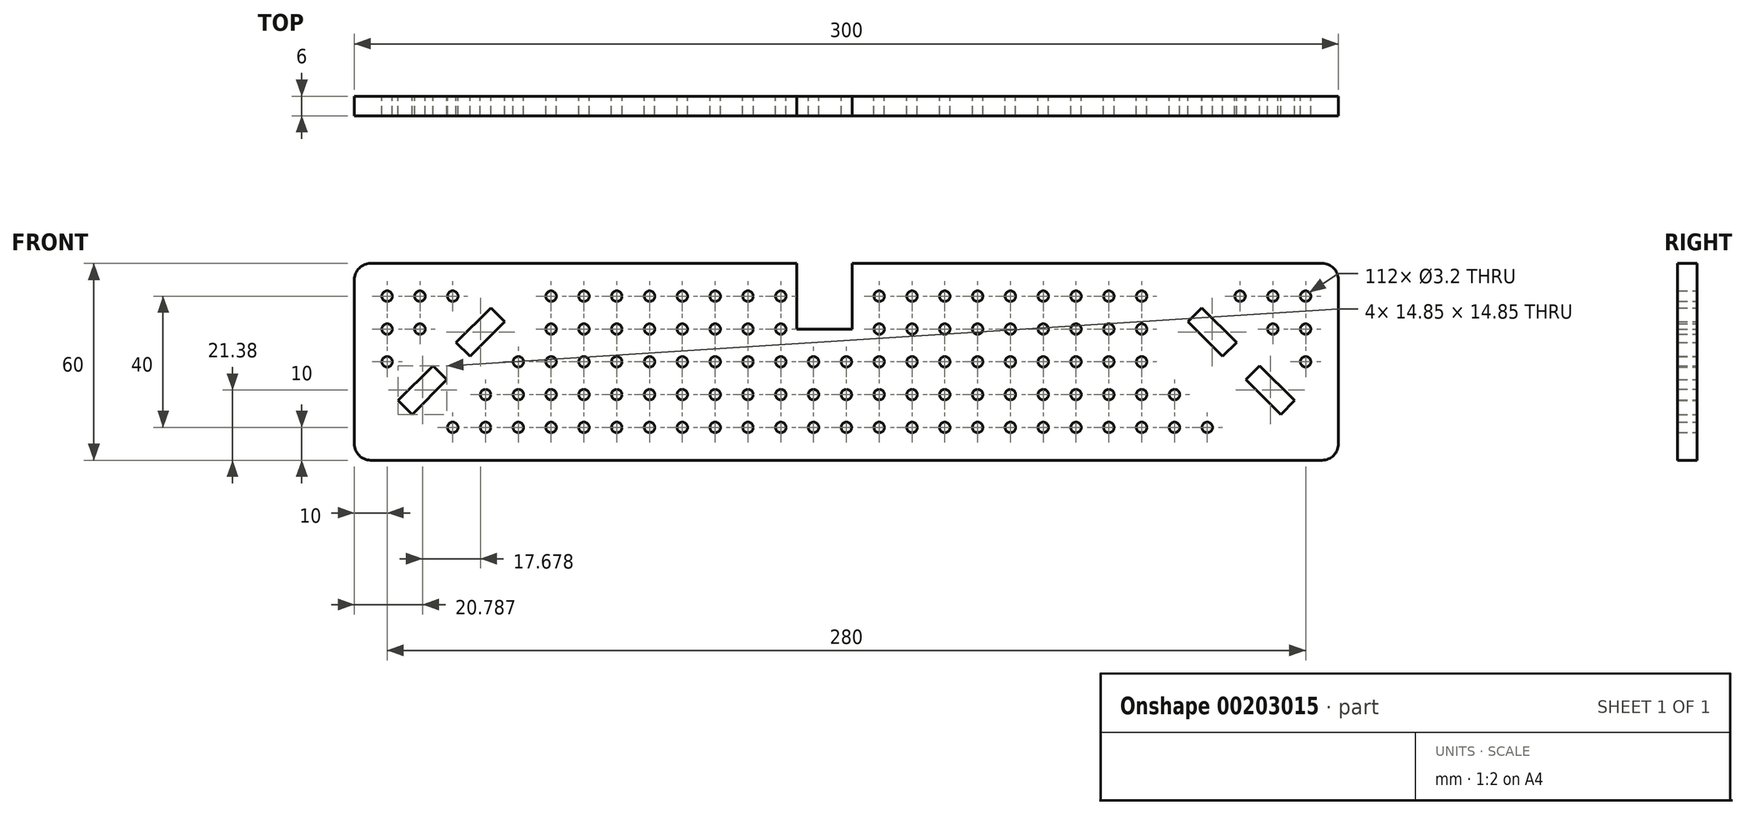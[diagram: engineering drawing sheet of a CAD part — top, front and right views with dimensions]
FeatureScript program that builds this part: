
annotation { "Feature Type Name" : "Feature", "Feature Type Description" : "" }
export const myFeature = defineFeature(function(context is Context, id is Id, definition is map)
    precondition{}
    {
        {
            var Q0;
            Q0=qCreatedBy(makeId("Front.planeOp"),FACE);
            var sketch = newSketch(context, id + "F0", { "sketchPlane" : qUnion([Q0])});
            skLineSegment(sketch, "E0", {"start": v(-150, -25) * mm, "end": v(-150, 25) * mm});
            skArc(sketch, "E1", {"start": v(-150, 25) * mm, "mid": v(-148.54, 28.54) * mm, "end": v(-145, 30) * mm});
            skLineSegment(sketch, "E2", {"start": v(-145, 30) * mm, "end": v(-15.18, 30) * mm});
            skArc(sketch, "E3", {"start": v(145, 30) * mm, "mid": v(148.54, 28.54) * mm, "end": v(150, 25) * mm});
            skLineSegment(sketch, "E4", {"start": v(150, 25) * mm, "end": v(150, -25) * mm});
            skArc(sketch, "E5", {"start": v(150, -25) * mm, "mid": v(148.54, -28.54) * mm, "end": v(145, -30) * mm});
            skLineSegment(sketch, "E6", {"start": v(145, -30) * mm, "end": v(-145, -30) * mm});
            skArc(sketch, "E7", {"start": v(-145, -30) * mm, "mid": v(-148.54, -28.54) * mm, "end": v(-150, -25) * mm});
            skLineSegment(sketch, "E8", {"start": v(-126.03, -1.2) * mm, "end": v(-136.64, -11.8) * mm});
            skLineSegment(sketch, "E9", {"start": v(-136.64, -11.8) * mm, "end": v(-132.4, -16.04) * mm});
            skLineSegment(sketch, "E10", {"start": v(-132.4, -16.04) * mm, "end": v(-121.79, -5.44) * mm});
            skLineSegment(sketch, "E11", {"start": v(-121.79, -5.44) * mm, "end": v(-126.03, -1.2) * mm});
            skLineSegment(sketch, "E12", {"start": v(-108.35, 16.48) * mm, "end": v(-118.96, 5.88) * mm});
            skLineSegment(sketch, "E13", {"start": v(-118.96, 5.88) * mm, "end": v(-114.72, 1.63) * mm});
            skLineSegment(sketch, "E14", {"start": v(-114.72, 1.63) * mm, "end": v(-104.11, 12.24) * mm});
            skLineSegment(sketch, "E15", {"start": v(-104.11, 12.24) * mm, "end": v(-108.35, 16.48) * mm});
            skCircle(sketch, "E16", {"center": v(-120, -20) * mm, "radius": 1.6 * mm});
            skCircle(sketch, "E17", {"center": v(-110, -20) * mm, "radius": 1.6 * mm});
            skCircle(sketch, "E18", {"center": v(-100, -20) * mm, "radius": 1.6 * mm});
            skCircle(sketch, "E19", {"center": v(-90, -20) * mm, "radius": 1.6 * mm});
            skCircle(sketch, "E20", {"center": v(-80, -20) * mm, "radius": 1.6 * mm});
            skCircle(sketch, "E21", {"center": v(-70, -20) * mm, "radius": 1.6 * mm});
            skCircle(sketch, "E22", {"center": v(-60, -20) * mm, "radius": 1.6 * mm});
            skCircle(sketch, "E23", {"center": v(-50, -20) * mm, "radius": 1.6 * mm});
            skCircle(sketch, "E24", {"center": v(-40, -20) * mm, "radius": 1.6 * mm});
            skCircle(sketch, "E25", {"center": v(-30, -20) * mm, "radius": 1.6 * mm});
            skCircle(sketch, "E26", {"center": v(-20, -20) * mm, "radius": 1.6 * mm});
            skCircle(sketch, "E27", {"center": v(-10, -20) * mm, "radius": 1.6 * mm});
            skCircle(sketch, "E28", {"center": v(0, -20) * mm, "radius": 1.6 * mm});
            skCircle(sketch, "E29", {"center": v(10, -20) * mm, "radius": 1.6 * mm});
            skCircle(sketch, "E30", {"center": v(20, -20) * mm, "radius": 1.6 * mm});
            skCircle(sketch, "E31", {"center": v(30, -20) * mm, "radius": 1.6 * mm});
            skCircle(sketch, "E32", {"center": v(40, -20) * mm, "radius": 1.6 * mm});
            skCircle(sketch, "E33", {"center": v(50, -20) * mm, "radius": 1.6 * mm});
            skCircle(sketch, "E34", {"center": v(60, -20) * mm, "radius": 1.6 * mm});
            skCircle(sketch, "E35", {"center": v(70, -20) * mm, "radius": 1.6 * mm});
            skCircle(sketch, "E36", {"center": v(80, -20) * mm, "radius": 1.6 * mm});
            skCircle(sketch, "E37", {"center": v(90, -20) * mm, "radius": 1.6 * mm});
            skCircle(sketch, "E38", {"center": v(100, -20) * mm, "radius": 1.6 * mm});
            skCircle(sketch, "E39", {"center": v(110, -20) * mm, "radius": 1.6 * mm});
            skCircle(sketch, "E40", {"center": v(-110, -10) * mm, "radius": 1.6 * mm});
            skCircle(sketch, "E41", {"center": v(-100, -10) * mm, "radius": 1.6 * mm});
            skCircle(sketch, "E42", {"center": v(-90, -10) * mm, "radius": 1.6 * mm});
            skCircle(sketch, "E43", {"center": v(-80, -10) * mm, "radius": 1.6 * mm});
            skCircle(sketch, "E44", {"center": v(-70, -10) * mm, "radius": 1.6 * mm});
            skCircle(sketch, "E45", {"center": v(-60, -10) * mm, "radius": 1.6 * mm});
            skCircle(sketch, "E46", {"center": v(-50, -10) * mm, "radius": 1.6 * mm});
            skCircle(sketch, "E47", {"center": v(-40, -10) * mm, "radius": 1.6 * mm});
            skCircle(sketch, "E48", {"center": v(-30, -10) * mm, "radius": 1.6 * mm});
            skCircle(sketch, "E49", {"center": v(-20, -10) * mm, "radius": 1.6 * mm});
            skCircle(sketch, "E50", {"center": v(-10, -10) * mm, "radius": 1.6 * mm});
            skCircle(sketch, "E51", {"center": v(0, -10) * mm, "radius": 1.6 * mm});
            skCircle(sketch, "E52", {"center": v(10, -10) * mm, "radius": 1.6 * mm});
            skCircle(sketch, "E53", {"center": v(20, -10) * mm, "radius": 1.6 * mm});
            skCircle(sketch, "E54", {"center": v(30, -10) * mm, "radius": 1.6 * mm});
            skCircle(sketch, "E55", {"center": v(40, -10) * mm, "radius": 1.6 * mm});
            skCircle(sketch, "E56", {"center": v(50, -10) * mm, "radius": 1.6 * mm});
            skCircle(sketch, "E57", {"center": v(60, -10) * mm, "radius": 1.6 * mm});
            skCircle(sketch, "E58", {"center": v(70, -10) * mm, "radius": 1.6 * mm});
            skCircle(sketch, "E59", {"center": v(80, -10) * mm, "radius": 1.6 * mm});
            skCircle(sketch, "E60", {"center": v(90, -10) * mm, "radius": 1.6 * mm});
            skCircle(sketch, "E61", {"center": v(100, -10) * mm, "radius": 1.6 * mm});
            skCircle(sketch, "E62", {"center": v(-140, 0) * mm, "radius": 1.6 * mm});
            skCircle(sketch, "E63", {"center": v(-100, 0) * mm, "radius": 1.6 * mm});
            skCircle(sketch, "E64", {"center": v(-90, 0) * mm, "radius": 1.6 * mm});
            skCircle(sketch, "E65", {"center": v(-80, 0) * mm, "radius": 1.6 * mm});
            skCircle(sketch, "E66", {"center": v(-70, 0) * mm, "radius": 1.6 * mm});
            skCircle(sketch, "E67", {"center": v(-60, 0) * mm, "radius": 1.6 * mm});
            skCircle(sketch, "E68", {"center": v(-50, 0) * mm, "radius": 1.6 * mm});
            skCircle(sketch, "E69", {"center": v(-40, 0) * mm, "radius": 1.6 * mm});
            skCircle(sketch, "E70", {"center": v(-30, 0) * mm, "radius": 1.6 * mm});
            skCircle(sketch, "E71", {"center": v(-20, 0) * mm, "radius": 1.6 * mm});
            skCircle(sketch, "E72", {"center": v(-10, 0) * mm, "radius": 1.6 * mm});
            skCircle(sketch, "E73", {"center": v(0, 0) * mm, "radius": 1.6 * mm});
            skCircle(sketch, "E74", {"center": v(10, 0) * mm, "radius": 1.6 * mm});
            skCircle(sketch, "E75", {"center": v(20, 0) * mm, "radius": 1.6 * mm});
            skCircle(sketch, "E76", {"center": v(30, 0) * mm, "radius": 1.6 * mm});
            skCircle(sketch, "E77", {"center": v(40, 0) * mm, "radius": 1.6 * mm});
            skCircle(sketch, "E78", {"center": v(50, 0) * mm, "radius": 1.6 * mm});
            skCircle(sketch, "E79", {"center": v(60, 0) * mm, "radius": 1.6 * mm});
            skCircle(sketch, "E80", {"center": v(70, 0) * mm, "radius": 1.6 * mm});
            skCircle(sketch, "E81", {"center": v(80, 0) * mm, "radius": 1.6 * mm});
            skCircle(sketch, "E82", {"center": v(90, 0) * mm, "radius": 1.6 * mm});
            skCircle(sketch, "E83", {"center": v(140, 0) * mm, "radius": 1.6 * mm});
            skCircle(sketch, "E84", {"center": v(-140, 10) * mm, "radius": 1.6 * mm});
            skCircle(sketch, "E85", {"center": v(-130, 10) * mm, "radius": 1.6 * mm});
            skCircle(sketch, "E86", {"center": v(-90, 10) * mm, "radius": 1.6 * mm});
            skCircle(sketch, "E87", {"center": v(-80, 10) * mm, "radius": 1.6 * mm});
            skCircle(sketch, "E88", {"center": v(-70, 10) * mm, "radius": 1.6 * mm});
            skCircle(sketch, "E89", {"center": v(-60, 10) * mm, "radius": 1.6 * mm});
            skCircle(sketch, "E90", {"center": v(-50, 10) * mm, "radius": 1.6 * mm});
            skCircle(sketch, "E91", {"center": v(-40, 10) * mm, "radius": 1.6 * mm});
            skCircle(sketch, "E92", {"center": v(-30, 10) * mm, "radius": 1.6 * mm});
            skCircle(sketch, "E93", {"center": v(-20, 10) * mm, "radius": 1.6 * mm});
            skCircle(sketch, "E94", {"center": v(10, 10) * mm, "radius": 1.6 * mm});
            skCircle(sketch, "E95", {"center": v(20, 10) * mm, "radius": 1.6 * mm});
            skCircle(sketch, "E96", {"center": v(30, 10) * mm, "radius": 1.6 * mm});
            skCircle(sketch, "E97", {"center": v(40, 10) * mm, "radius": 1.6 * mm});
            skCircle(sketch, "E98", {"center": v(50, 10) * mm, "radius": 1.6 * mm});
            skCircle(sketch, "E99", {"center": v(60, 10) * mm, "radius": 1.6 * mm});
            skCircle(sketch, "E100", {"center": v(70, 10) * mm, "radius": 1.6 * mm});
            skCircle(sketch, "E101", {"center": v(80, 10) * mm, "radius": 1.6 * mm});
            skCircle(sketch, "E102", {"center": v(90, 10) * mm, "radius": 1.6 * mm});
            skCircle(sketch, "E103", {"center": v(130, 10) * mm, "radius": 1.6 * mm});
            skCircle(sketch, "E104", {"center": v(140, 10) * mm, "radius": 1.6 * mm});
            skCircle(sketch, "E105", {"center": v(-140, 20) * mm, "radius": 1.6 * mm});
            skCircle(sketch, "E106", {"center": v(-130, 20) * mm, "radius": 1.6 * mm});
            skCircle(sketch, "E107", {"center": v(-120, 20) * mm, "radius": 1.6 * mm});
            skCircle(sketch, "E108", {"center": v(-90, 20) * mm, "radius": 1.6 * mm});
            skCircle(sketch, "E109", {"center": v(-80, 20) * mm, "radius": 1.6 * mm});
            skCircle(sketch, "E110", {"center": v(-70, 20) * mm, "radius": 1.6 * mm});
            skCircle(sketch, "E111", {"center": v(-60, 20) * mm, "radius": 1.6 * mm});
            skCircle(sketch, "E112", {"center": v(-50, 20) * mm, "radius": 1.6 * mm});
            skCircle(sketch, "E113", {"center": v(-40, 20) * mm, "radius": 1.6 * mm});
            skCircle(sketch, "E114", {"center": v(-30, 20) * mm, "radius": 1.6 * mm});
            skCircle(sketch, "E115", {"center": v(-20, 20) * mm, "radius": 1.6 * mm});
            skCircle(sketch, "E116", {"center": v(10, 20) * mm, "radius": 1.6 * mm});
            skCircle(sketch, "E117", {"center": v(20, 20) * mm, "radius": 1.6 * mm});
            skCircle(sketch, "E118", {"center": v(30, 20) * mm, "radius": 1.6 * mm});
            skCircle(sketch, "E119", {"center": v(40, 20) * mm, "radius": 1.6 * mm});
            skCircle(sketch, "E120", {"center": v(50, 20) * mm, "radius": 1.6 * mm});
            skCircle(sketch, "E121", {"center": v(60, 20) * mm, "radius": 1.6 * mm});
            skCircle(sketch, "E122", {"center": v(70, 20) * mm, "radius": 1.6 * mm});
            skCircle(sketch, "E123", {"center": v(80, 20) * mm, "radius": 1.6 * mm});
            skCircle(sketch, "E124", {"center": v(90, 20) * mm, "radius": 1.6 * mm});
            skCircle(sketch, "E125", {"center": v(120, 20) * mm, "radius": 1.6 * mm});
            skCircle(sketch, "E126", {"center": v(130, 20) * mm, "radius": 1.6 * mm});
            skCircle(sketch, "E127", {"center": v(140, 20) * mm, "radius": 1.6 * mm});
            skLineSegment(sketch, "E128", {"start": v(126.03, -1.2) * mm, "end": v(136.64, -11.8) * mm});
            skLineSegment(sketch, "E129", {"start": v(136.64, -11.8) * mm, "end": v(132.4, -16.04) * mm});
            skLineSegment(sketch, "E130", {"start": v(132.4, -16.04) * mm, "end": v(121.79, -5.44) * mm});
            skLineSegment(sketch, "E131", {"start": v(121.79, -5.44) * mm, "end": v(126.03, -1.2) * mm});
            skLineSegment(sketch, "E132", {"start": v(108.35, 16.48) * mm, "end": v(118.96, 5.88) * mm});
            skLineSegment(sketch, "E133", {"start": v(118.96, 5.88) * mm, "end": v(114.72, 1.63) * mm});
            skLineSegment(sketch, "E134", {"start": v(114.72, 1.63) * mm, "end": v(104.11, 12.24) * mm});
            skLineSegment(sketch, "E135", {"start": v(104.11, 12.24) * mm, "end": v(108.35, 16.48) * mm});
            skLineSegment(sketch, "E136", {"start": v(-15.18, 10) * mm, "end": v(-15.18, 30) * mm});
            skLineSegment(sketch, "E137", {"start": v(1.82, 30) * mm, "end": v(1.82, 10) * mm});
            skLineSegment(sketch, "E138", {"start": v(1.82, 10) * mm, "end": v(-15.18, 10) * mm});
            skLineSegment(sketch, "E139.trimOffspring", {"start": v(1.82, 30) * mm, "end": v(145, 30) * mm});
            skSolve(sketch);
        }
        {
            assignVariable(context, id + "F1", {"name" : "ta", "anyValue" : 6});
        }
        {
            var Q0;
            Q0 = qSketchRegion(id + "F0", true);
            extrude(context, id + "F2", {"entities" : qUnion([Q0]), "depth" : (getVariable(context, 'ta')) * mm});
        }
    });
